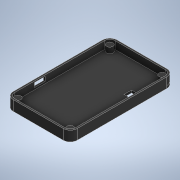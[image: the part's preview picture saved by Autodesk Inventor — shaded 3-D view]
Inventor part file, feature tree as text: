
AUTODESK INVENTOR PART (.ipt)
format: ipt  version: 2022 (Build 260153000, 153)  size: 187,392 bytes
history: native  units: mm
features: extrude x4, sketch x4, other x1
ambient origin geometry x8: Origin, YZ Plane, XZ Plane, XY Plane, X Axis, Y Axis, Z Axis, Center Point
bodies: Body1 (feature_tree)
feature tree (9):
  other  "Твердое тело1"
  extrude  "Выдавливание1"  Depth=5.0mm
  extrude  "Выдавливание2"  Depth=5.0mm
  extrude  "Выдавливание3"  Depth=5.0mm
  extrude  "Выдавливание4"  Depth=5.0mm
  sketch  "Эскиз1"
  sketch  "Эскиз3"
  sketch  "Эскиз4"
  sketch  "Эскиз5"
